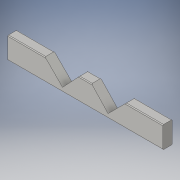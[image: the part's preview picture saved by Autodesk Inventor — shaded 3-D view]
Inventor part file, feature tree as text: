
AUTODESK INVENTOR PART (.ipt)
format: ipt  version: 2016 (Build 200138000, 138)  size: 121,344 bytes
history: native  units: in
note: dims shown in document units (in); Inventor stores cm internally (conversion verified against a paired STEP export)
features: extrude x1, fillet x1, sketch x1
ambient origin geometry x8: Origin, YZ Plane, XZ Plane, XY Plane, X Axis, Y Axis, Z Axis, Center Point
bodies: Solid1 (feature_tree)
feature tree (3):
  extrude  "Extrusion1"  Depth=3.5in
  fillet  "Fillet1"  Radius=3.5in
  sketch  "Sketch1"  dims[d0=25.0in d1=3.5in d2=3.5in d3=6.0in d4=6.0in d5=1.0in d6=1.0in d7=4.0in d8=135.0deg d9=4.0in d10=45.0deg d11=1.5in d12=0.0in d13=0.125in]
